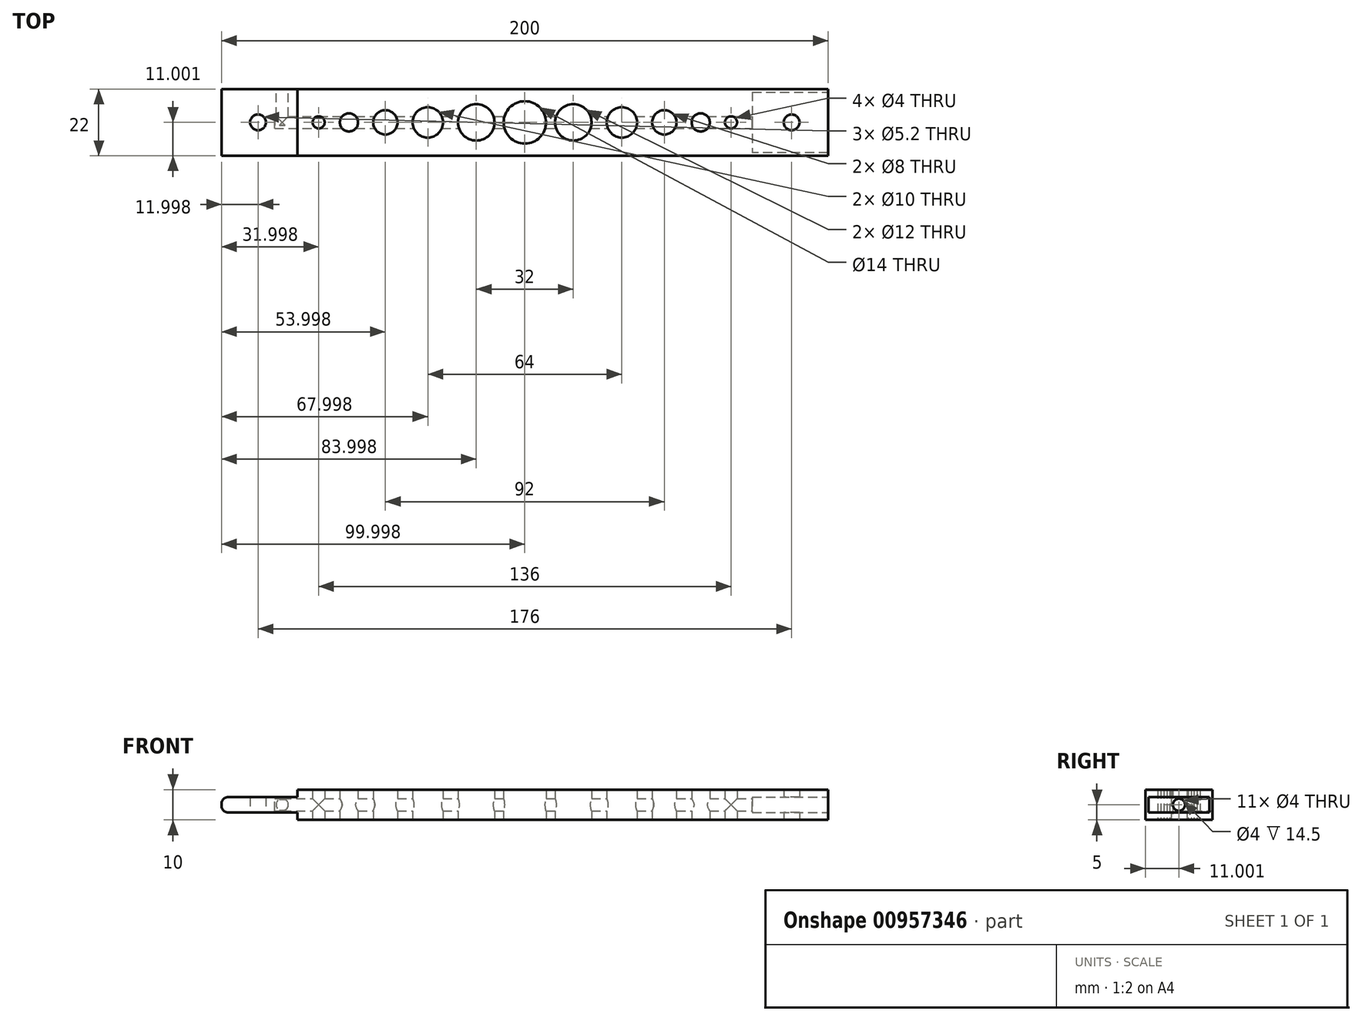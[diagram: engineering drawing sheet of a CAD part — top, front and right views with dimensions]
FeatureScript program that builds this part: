
annotation { "Feature Type Name" : "Feature", "Feature Type Description" : "" }
export const myFeature = defineFeature(function(context is Context, id is Id, definition is map)
    precondition{}
    {
        {
            var Q0;
            Q0=qCreatedBy(makeId("Top.planeOp"),FACE);
            var sketch = newSketch(context, id + "F0", { "sketchPlane" : qUnion([Q0])});
            skLineSegment(sketch, "E0.bottom", {"start": v(-72.7, 35.51) * mm, "end": v(127.3, 35.51) * mm});
            skLineSegment(sketch, "E0.top", {"start": v(-72.7, 13.51) * mm, "end": v(127.3, 13.51) * mm});
            skLineSegment(sketch, "E0.left", {"start": v(-72.7, 35.51) * mm, "end": v(-72.7, 13.51) * mm});
            skLineSegment(sketch, "E0.right", {"start": v(127.3, 35.51) * mm, "end": v(127.3, 13.51) * mm});
            skCircle(sketch, "E1", {"center": v(-60.7, 24.51) * mm, "radius": 2.6 * mm});
            skPoint(sketch, "E1.centerSnap0", {"position": v(-72.7, 24.51) * mm});
            skCircle(sketch, "E2", {"center": v(115.3, 24.51) * mm, "radius": 2.6 * mm});
            skPoint(sketch, "E2.centerSnap0", {"position": v(127.3, 24.51) * mm});
            skLineSegment(sketch, "E3", {"start": v(-47.7, 35.51) * mm, "end": v(-47.7, 13.51) * mm});
            skLineSegment(sketch, "E4", {"start": v(102.3, 35.51) * mm, "end": v(102.3, 13.51) * mm});
            skCircle(sketch, "E5", {"center": v(-40.7, 24.51) * mm, "radius": 2 * mm});
            skCircle(sketch, "E6", {"center": v(-30.7, 24.51) * mm, "radius": 3 * mm});
            skCircle(sketch, "E7", {"center": v(-18.7, 24.51) * mm, "radius": 4 * mm});
            skCircle(sketch, "E8", {"center": v(-4.7, 24.51) * mm, "radius": 5 * mm});
            skCircle(sketch, "E9", {"center": v(11.3, 24.51) * mm, "radius": 6 * mm});
            skCircle(sketch, "E10", {"center": v(27.3, 24.51) * mm, "radius": 7 * mm});
            skCircle(sketch, "E11", {"center": v(43.3, 24.51) * mm, "radius": 6 * mm});
            skCircle(sketch, "E12", {"center": v(59.3, 24.51) * mm, "radius": 5 * mm});
            skCircle(sketch, "E13", {"center": v(73.3, 24.51) * mm, "radius": 4 * mm});
            skCircle(sketch, "E14", {"center": v(85.3, 24.51) * mm, "radius": 3 * mm});
            skCircle(sketch, "E15", {"center": v(95.3, 24.51) * mm, "radius": 2 * mm});
            skLineSegment(sketch, "E16", {"start": v(-72.7, 24.51) * mm, "end": v(127.3, 24.51) * mm, "construction": true});
            skLineSegment(sketch, "E17", {"start": v(102.3, 34.51) * mm, "end": v(127.3, 34.51) * mm});
            skLineSegment(sketch, "E18", {"start": v(127.3, 14.51) * mm, "end": v(102.3, 14.51) * mm});
            skSolve(sketch);
        }
        {
            var Q0;
            {var subQ0=sQuery(id+"F0.wireOp",EDGE,"E3");Q0=makeQuery(id+"F0.imprint","IMPRINT",FACE,{"disambiguationData":[TD([[makeQuery(id+"F0.imprint","IMPRINT",EDGE,{"derivedFrom":subQ0}),1.0]])]});}
            extrude(context, id + "F1", {"entities" : qUnion([Q0]), "depth" : 10 * mm, "offsetDistance" : 25 * mm});
        }
        {
            var Q0;
            {var subQ0=sQuery(id+"F0.wireOp",EDGE,"E0.left");Q0=makeQuery(id+"F0.imprint","IMPRINT",FACE,{"disambiguationData":[TD([[makeQuery(id+"F0.imprint","IMPRINT",EDGE,{"derivedFrom":subQ0}),1.0]])]});}
            extrude(context, id + "F2", {"entities" : qUnion([Q0]), "operationType" : NewBodyOperationType.ADD, "depth" : 7.5 * mm, "offsetDistance" : 25 * mm, "hasSecondDirection" : true, "secondDirectionOppositeDirection" : false, "secondDirectionDepth" : 2.5 * mm});
        }
        {
            var Q0;
            {var subQ0=sQuery(id+"F0.wireOp",EDGE,"E0.right");Q0=makeQuery(id+"F0.imprint","IMPRINT",FACE,{"disambiguationData":[TD([[makeQuery(id+"F0.imprint","IMPRINT",EDGE,{"derivedFrom":subQ0}),-1.0]])]});}
            extrude(context, id + "F3", {"entities" : qUnion([Q0]), "operationType" : NewBodyOperationType.ADD, "depth" : 2.5 * mm, "offsetDistance" : 25 * mm, "hasSecondDirection" : true, "secondDirectionOppositeDirection" : false, "secondDirectionDepth" : 0 * mm});
        }
        {
            var Q0;
            {var subQ0=sQuery(id+"F0.wireOp",EDGE,"E0.right");Q0=makeQuery(id+"F0.imprint","IMPRINT",FACE,{"disambiguationData":[TD([[makeQuery(id+"F0.imprint","IMPRINT",EDGE,{"derivedFrom":subQ0}),-1.0]])]});}
            extrude(context, id + "F4", {"entities" : qUnion([Q0]), "operationType" : NewBodyOperationType.ADD, "depth" : 10 * mm, "offsetDistance" : 25 * mm});
        }
        {
            var Q0;
            Q0=makeQuery(id+"F2.opExtrude","CAP_EDGE",EDGE,{"disambiguationData":[OSD([sQuery(id+"F0.wireOp",EDGE,"E0.left")])],"isStart":false});
            var Q1;
            Q1=makeQuery(id+"F2.opExtrude","CAP_EDGE",EDGE,{"disambiguationData":[OSD([sQuery(id+"F0.wireOp",EDGE,"E0.left")])],"isStart":true});
            fillet(context, id + "F5", {"entities" : qUnion([Q0, Q1]), "radius" : 2 * mm, "tangentPropagation" : true, "allowEdgeOverflow" : false});
        }
        {
            var Q0;
            Q0=makeQuery(id+"F1.opExtrude","SWEPT_FACE",FACE,{"disambiguationData":[OSD([sQuery(id+"F0.wireOp",EDGE,"E4")])]});
            var sketch = newSketch(context, id + "F6", { "sketchPlane" : qUnion([Q0])});
            skPoint(sketch, "E19.centerSnap0", {"position": v(35.01, 2.5) * mm});
            skLineSegment(sketch, "E20", {"start": v(13.51, 5) * mm, "end": v(35.51, 5) * mm, "construction": true});
            skLineSegment(sketch, "E21", {"start": v(24.51, 10) * mm, "end": v(24.51, 0) * mm, "construction": true});
            skCircle(sketch, "E22", {"center": v(24.51, 5) * mm, "radius": 2 * mm});
            skSolve(sketch);
        }
        {
            var Q0;
            Q0=makeQuery(id+"F6.imprint","IMPRINT",FACE,{"disambiguationData":[TD([[makeQuery(id+"F6.imprint","IMPRINT",EDGE,{"derivedFrom":sQuery(id+"F6.wireOp",EDGE,"E22")}),1.0]])]});
            extrude(context, id + "F7", {"entities" : qUnion([Q0]), "operationType" : NewBodyOperationType.REMOVE, "oppositeDirection" : true, "depth" : 157.5 * mm, "offsetDistance" : 25 * mm});
        }
        {
            var Q0;
            {var subQ0=sQuery(id+"F0.wireOp",EDGE,"E0.bottom");Q0=makeQuery(id+"F4.boolean.opBoolean","MERGE",FACE,{"derivedFrom":[makeQuery(id+"F3.boolean.opBoolean","MERGE",FACE,{"derivedFrom":[makeQuery(id+"F2.boolean.opBoolean","MERGE",FACE,{"derivedFrom":[makeQuery(id+"F1.opExtrude","SWEPT_FACE",FACE,{"disambiguationData":[OSD([subQ0])]}),makeQuery(id+"F2.opExtrude","SWEPT_FACE",FACE,{"disambiguationData":[OSD([subQ0])]})]}),makeQuery(id+"F3.opExtrude","SWEPT_FACE",FACE,{"disambiguationData":[OSD([subQ0])]})]}),makeQuery(id+"F4.opExtrude","SWEPT_FACE",FACE,{"disambiguationData":[OSD([subQ0])]})]});}
            var sketch = newSketch(context, id + "F8", { "sketchPlane" : qUnion([Q0])});
            skCircle(sketch, "E23", {"center": v(52.7, 5) * mm, "radius": 2 * mm});
            skSolve(sketch);
        }
        {
            var Q0;
            Q0=makeQuery(id+"F8.imprint","IMPRINT",FACE,{"disambiguationData":[TD([[makeQuery(id+"F8.imprint","IMPRINT",EDGE,{"derivedFrom":sQuery(id+"F8.wireOp",EDGE,"E23")}),1.0]])]});
            extrude(context, id + "F9", {"entities" : qUnion([Q0]), "operationType" : NewBodyOperationType.REMOVE, "oppositeDirection" : true, "depth" : 12 * mm, "offsetDistance" : 25 * mm});
        }
        {
            var Q0;
            Q0=makeQuery(id+"F0.imprint","IMPRINT",FACE,{"disambiguationData":[TD([[makeQuery(id+"F0.imprint","IMPRINT",EDGE,{"derivedFrom":sQuery(id+"F0.wireOp",EDGE,"E2")}),-1.0]])]});
            extrude(context, id + "F10", {"entities" : qUnion([Q0]), "operationType" : NewBodyOperationType.ADD, "depth" : 2.5 * mm, "offsetDistance" : 25 * mm});
        }
        {
            var Q0;
            Q0=makeQuery(id+"F0.imprint","IMPRINT",FACE,{"disambiguationData":[TD([[makeQuery(id+"F0.imprint","IMPRINT",EDGE,{"derivedFrom":sQuery(id+"F0.wireOp",EDGE,"E2")}),-1.0]])]});
            extrude(context, id + "F11", {"entities" : qUnion([Q0]), "operationType" : NewBodyOperationType.ADD, "depth" : 10 * mm, "offsetDistance" : 25 * mm, "hasSecondDirection" : true, "secondDirectionOppositeDirection" : false, "secondDirectionDepth" : 7.5 * mm});
        }
    });
